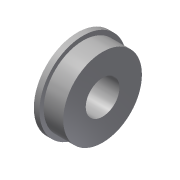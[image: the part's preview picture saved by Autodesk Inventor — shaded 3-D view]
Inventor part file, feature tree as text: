
AUTODESK INVENTOR PART (.ipt)
format: ipt  version: 2013 (Build 170138000, 138)  size: 118,784 bytes
history: native  units: in
note: dims shown in document units (in); Inventor stores cm internally (conversion verified against a paired STEP export)
features: revolve x1, imported_body x1
ambient origin geometry x8: Origin, YZ Plane, XZ Plane, XY Plane, X Axis, Y Axis, Z Axis, Center Point
feature tree (2):
  revolve  "Revolve1"  [1 undecoded]
  imported_body  "Base1"
note: 1 required parameter value undecoded (feature->parameter linkage not recoverable at this tier; creation-order binding heuristic only, values carry confidence <= 0.55)
